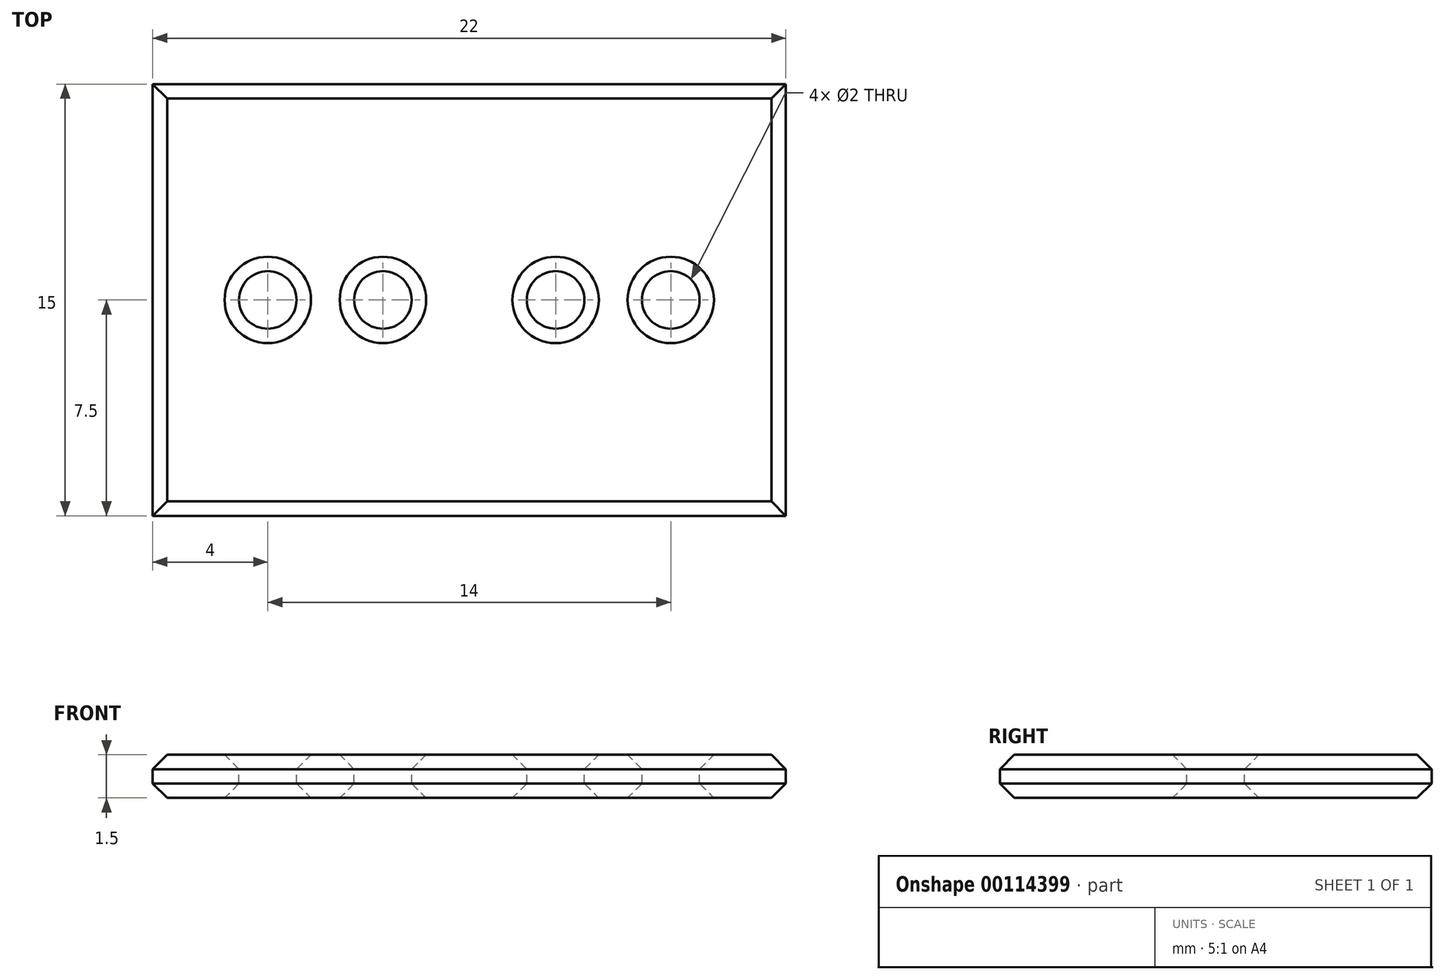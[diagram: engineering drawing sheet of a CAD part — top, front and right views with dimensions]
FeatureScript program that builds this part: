
annotation { "Feature Type Name" : "Feature", "Feature Type Description" : "" }
export const myFeature = defineFeature(function(context is Context, id is Id, definition is map)
    precondition{}
    {
        {
            var Q0;
            Q0=qCreatedBy(makeId("Top.planeOp"),FACE);
            var sketch = newSketch(context, id + "F0", { "sketchPlane" : qUnion([Q0])});
            skLineSegment(sketch, "E0.bottom", {"start": v(0, 0) * mm, "end": v(22, 0) * mm});
            skLineSegment(sketch, "E0.top", {"start": v(0, 15) * mm, "end": v(22, 15) * mm});
            skLineSegment(sketch, "E0.left", {"start": v(0, 0) * mm, "end": v(0, 15) * mm});
            skLineSegment(sketch, "E0.right", {"start": v(22, 0) * mm, "end": v(22, 15) * mm});
            skSolve(sketch);
        }
        {
            var Q0;
            Q0=makeQuery(id+"F0.imprint","IMPRINT",FACE,{"disambiguationData":[TD([[makeQuery(id+"F0.imprint","IMPRINT",EDGE,{"derivedFrom":sQuery(id+"F0.wireOp",EDGE,"E0.bottom")}),1.0]])]});
            extrude(context, id + "F1", {"entities" : qUnion([Q0]), "depth" : 1.5 * mm});
        }
        {
            var Q0;
            Q0=makeQuery(id+"F1.opExtrude","CAP_FACE",FACE,{"disambiguationData":[OSD([sQuery(id+"F0.wireOp",EDGE,"E0.bottom"),sQuery(id+"F0.wireOp",EDGE,"E0.top"),sQuery(id+"F0.wireOp",EDGE,"E0.left"),sQuery(id+"F0.wireOp",EDGE,"E0.right")])],"isStart":false});
            var sketch = newSketch(context, id + "F2", { "sketchPlane" : qUnion([Q0])});
            skLineSegment(sketch, "E1", {"start": v(0, 7.5) * mm, "end": v(22, 7.5) * mm, "construction": true});
            skCircle(sketch, "E2", {"center": v(4, 7.5) * mm, "radius": 1 * mm});
            skCircle(sketch, "E3", {"center": v(8, 7.5) * mm, "radius": 1 * mm});
            skCircle(sketch, "E4", {"center": v(14, 7.5) * mm, "radius": 1 * mm});
            skCircle(sketch, "E5", {"center": v(18, 7.5) * mm, "radius": 1 * mm});
            skSolve(sketch);
        }
        {
            var Q0;
            Q0 = qSketchRegion(id + "F2", true);
            extrude(context, id + "F3", {"entities" : qUnion([Q0]), "operationType" : NewBodyOperationType.REMOVE, "endBound" : BoundingType.THROUGH_ALL, "oppositeDirection" : true, "depth" : 25 * mm});
        }
        {
            var Q0;
            Q0=makeQuery(id+"F1.opExtrude","CAP_FACE",FACE,{"disambiguationData":[OSD([sQuery(id+"F0.wireOp",EDGE,"E0.bottom"),sQuery(id+"F0.wireOp",EDGE,"E0.top"),sQuery(id+"F0.wireOp",EDGE,"E0.left"),sQuery(id+"F0.wireOp",EDGE,"E0.right")])],"isStart":false});
            var Q1;
            Q1=makeQuery(id+"F1.opExtrude","CAP_FACE",FACE,{"disambiguationData":[OSD([sQuery(id+"F0.wireOp",EDGE,"E0.bottom"),sQuery(id+"F0.wireOp",EDGE,"E0.top"),sQuery(id+"F0.wireOp",EDGE,"E0.left"),sQuery(id+"F0.wireOp",EDGE,"E0.right")])],"isStart":true});
            chamfer(context, id + "F4", {"entities" : qUnion([Q0, Q1]), "width" : 0.5 * mm, "tangentPropagation" : true});
        }
    });
